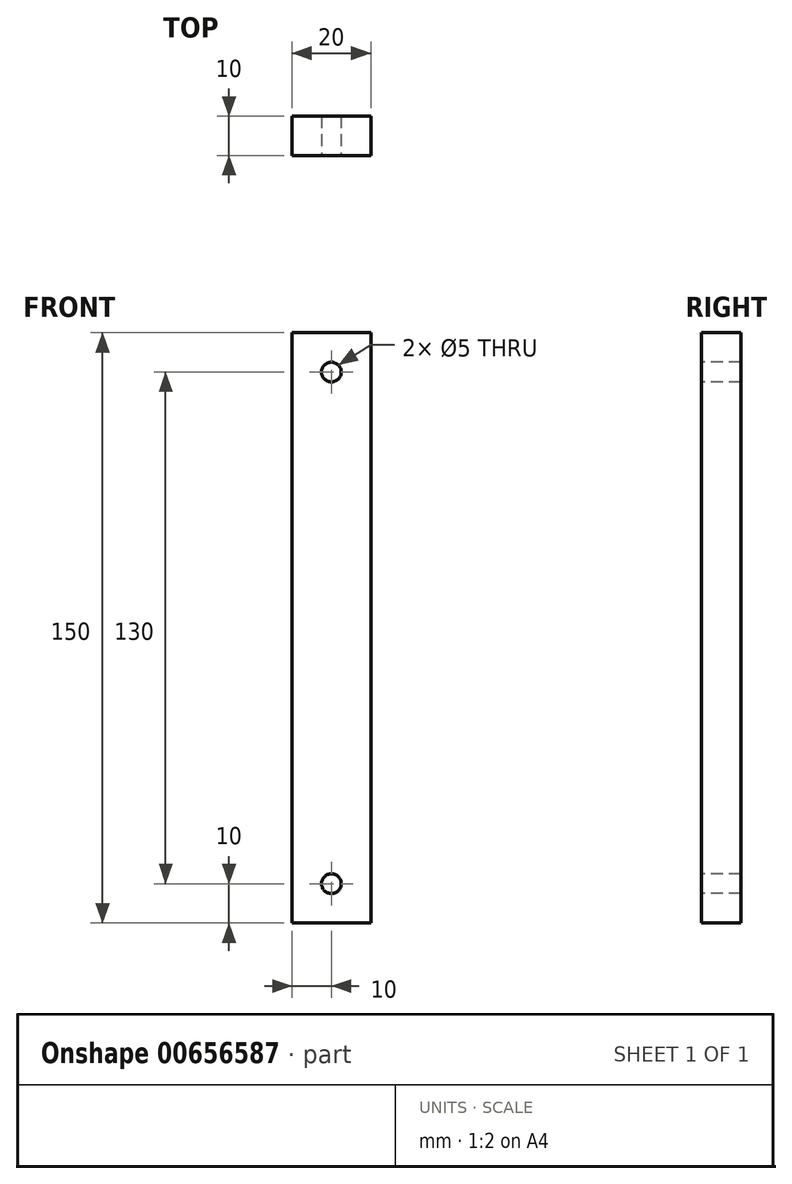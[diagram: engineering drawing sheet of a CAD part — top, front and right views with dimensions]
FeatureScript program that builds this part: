
annotation { "Feature Type Name" : "Feature", "Feature Type Description" : "" }
export const myFeature = defineFeature(function(context is Context, id is Id, definition is map)
    precondition{}
    {
        {
            var Q0;
            Q0=qCreatedBy(makeId("Front.planeOp"),FACE);
            var sketch = newSketch(context, id + "F0", { "sketchPlane" : qUnion([Q0])});
            skLineSegment(sketch, "E0.bottom", {"start": v(0, 0) * mm, "end": v(20, 0) * mm});
            skLineSegment(sketch, "E0.top", {"start": v(0, 150) * mm, "end": v(20, 150) * mm});
            skLineSegment(sketch, "E0.left", {"start": v(0, 0) * mm, "end": v(0, 150) * mm});
            skLineSegment(sketch, "E0.right", {"start": v(20, 0) * mm, "end": v(20, 150) * mm});
            skSolve(sketch);
        }
        {
            var Q0;
            Q0=qSketchRegion(id+"F0",true);
            extrude(context, id + "F1", {"entities" : qUnion([Q0]), "depth" : 10 * mm, "offsetDistance" : 25 * mm});
        }
        {
            var Q0;
            Q0=makeQuery(id+"F1.opExtrude","CAP_FACE",FACE,{"disambiguationData":[OSD([sQuery(id+"F0.wireOp",EDGE,"E0.bottom"),sQuery(id+"F0.wireOp",EDGE,"E0.top"),sQuery(id+"F0.wireOp",EDGE,"E0.left"),sQuery(id+"F0.wireOp",EDGE,"E0.right")])],"isStart":false});
            var sketch = newSketch(context, id + "F2", { "sketchPlane" : qUnion([Q0])});
            skPoint(sketch, "E1", {"position": v(10, 140) * mm});
            skPoint(sketch, "E2", {"position": v(10, 10) * mm});
            skSolve(sketch);
        }
        {
            var Q0;
            Q0=sQuery(id+"F2.wireOp",VERTEX,"E1");
            var Q1;
            Q1=sQuery(id+"F2.wireOp",VERTEX,"E2");
            var Q2;
            Q2=makeQuery(id+"F1.opExtrude","SWEPT_BODY",BODY,{"disambiguationData":[OSD([sQuery(id+"F0.wireOp",EDGE,"E0.bottom"),sQuery(id+"F0.wireOp",EDGE,"E0.top"),sQuery(id+"F0.wireOp",EDGE,"E0.left"),sQuery(id+"F0.wireOp",EDGE,"E0.right")])]});
            hole(context, id + "F3", {"style" : HoleStyle.SIMPLE, "endStyle" : HoleEndStyle.THROUGH, "holeDiameter" : 5 * mm, "majorDiameter" : 5 * mm, "isTappedThrough" : true, "tappedDepth" : 12 * mm, "tapClearance" : 3, "locations" : qUnion([Q0, Q1]), "scope" : qUnion([Q2])});
        }
    });
